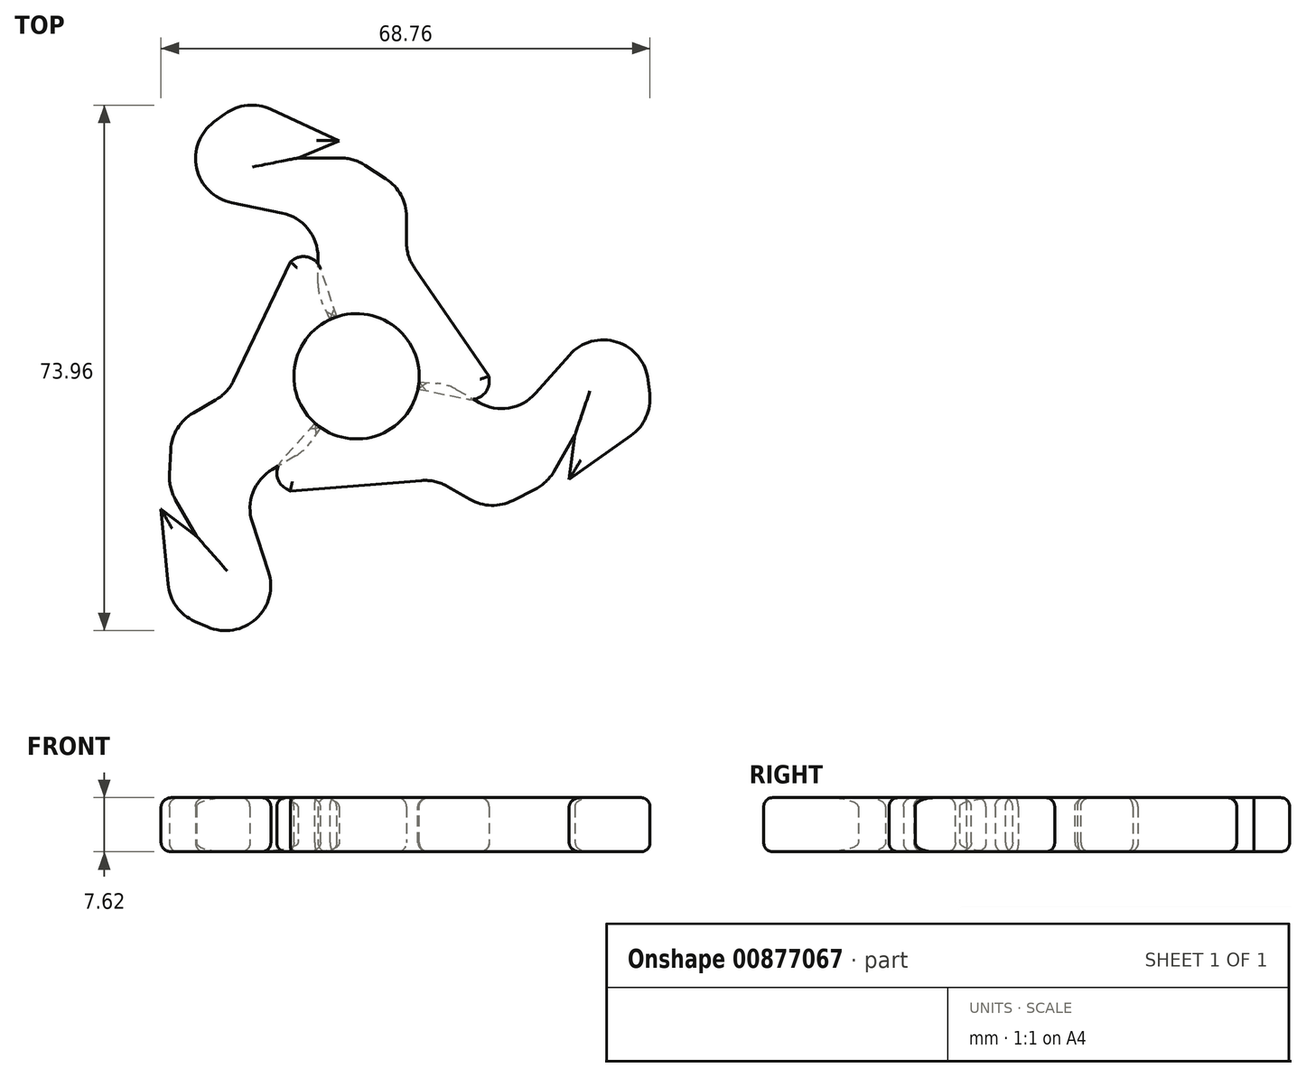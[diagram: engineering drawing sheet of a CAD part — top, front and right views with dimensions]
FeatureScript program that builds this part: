
annotation { "Feature Type Name" : "Feature", "Feature Type Description" : "" }
export const myFeature = defineFeature(function(context is Context, id is Id, definition is map)
    precondition{}
    {
        {
            var Q0;
            Q0=qCreatedBy(makeId("Top.planeOp"),FACE);
            var sketch = newSketch(context, id + "F0", { "sketchPlane" : qUnion([Q0])});
            skLineSegment(sketch, "E0", {"start": v(-31.2, 32.55) * mm, "end": v(-29.62, 33.7) * mm});
            skLineSegment(sketch, "E1", {"start": v(-23.2, 34.37) * mm, "end": v(-13.55, 29.92) * mm});
            skLineSegment(sketch, "E2", {"start": v(-13.55, 29.92) * mm, "end": v(-19.38, 27.5) * mm});
            skLineSegment(sketch, "E3", {"start": v(-19.38, 27.5) * mm, "end": v(-13.42, 27.5) * mm});
            skLineSegment(sketch, "E4", {"start": v(-9.97, 26.48) * mm, "end": v(-7.01, 24.57) * mm});
            skLineSegment(sketch, "E5", {"start": v(-4.12, 19.24) * mm, "end": v(-4.12, 15.63) * mm});
            skLineSegment(sketch, "E6", {"start": v(-3, 12.03) * mm, "end": v(7.5, -3.22) * mm});
            skLineSegment(sketch, "E7", {"start": v(7.5, -3.22) * mm, "end": v(-11.14, -3.22) * mm});
            skLineSegment(sketch, "E8", {"start": v(-11.14, -3.22) * mm, "end": v(-15.97, 7.16) * mm});
            skLineSegment(sketch, "E9", {"start": v(-16.56, 9.84) * mm, "end": v(-16.56, 13.55) * mm});
            skLineSegment(sketch, "E10", {"start": v(-21.64, 19.77) * mm, "end": v(-28.7, 21.22) * mm});
            skLineSegment(sketch, "E11", {"start": v(-11.14, -3.22) * mm, "end": v(4.46, -6.42) * mm});
            skLineSegment(sketch, "E12", {"start": v(7.51, -3.86) * mm, "end": v(7.5, -3.22) * mm});
            skPoint(sketch, "E13.visualSharp", {"position": v(-16.56, 18.73) * mm});
            skArc(sketch, "E13.filletArc", {"start": v(-16.56, 13.55) * mm, "mid": v(-18, 17.56) * mm, "end": v(-21.64, 19.77) * mm});
            skPoint(sketch, "E14.visualSharp", {"position": v(-16.56, 8.43) * mm});
            skArc(sketch, "E14.filletArc", {"start": v(-16.56, 9.84) * mm, "mid": v(-16.41, 8.47) * mm, "end": v(-15.97, 7.16) * mm});
            skPoint(sketch, "E15.visualSharp", {"position": v(-4.12, 13.65) * mm});
            skArc(sketch, "E15.filletArc", {"start": v(-4.12, 15.63) * mm, "mid": v(-3.83, 13.74) * mm, "end": v(-3, 12.03) * mm});
            skPoint(sketch, "E16.visualSharp", {"position": v(-4.12, 22.69) * mm});
            skArc(sketch, "E16.filletArc", {"start": v(-4.12, 19.24) * mm, "mid": v(-4.89, 22.27) * mm, "end": v(-7.01, 24.57) * mm});
            skPoint(sketch, "E17.visualSharp", {"position": v(-11.54, 27.5) * mm});
            skArc(sketch, "E17.filletArc", {"start": v(-9.97, 26.48) * mm, "mid": v(-11.62, 27.25) * mm, "end": v(-13.42, 27.5) * mm});
            skPoint(sketch, "E18.visualSharp", {"position": v(-26.6, 35.94) * mm});
            skArc(sketch, "E18.filletArc", {"start": v(-23.2, 34.37) * mm, "mid": v(-26.5, 34.92) * mm, "end": v(-29.62, 33.7) * mm});
            skPoint(sketch, "E19.visualSharp", {"position": v(7.6, -7.07) * mm});
            skArc(sketch, "E19.filletArc", {"start": v(4.46, -6.42) * mm, "mid": v(6.6, -5.88) * mm, "end": v(7.51, -3.86) * mm});
            skPoint(sketch, "E20.visualSharp", {"position": v(-42.67, 24.08) * mm});
            skArc(sketch, "E20.filletArc", {"start": v(-31.2, 32.55) * mm, "mid": v(-33.63, 26.07) * mm, "end": v(-28.7, 21.22) * mm});
            skSolve(sketch);
        }
        {
            var Q0;
            Q0=makeQuery(id+"F0.imprint","IMPRINT",FACE,{"disambiguationData":[TD([[makeQuery(id+"F0.imprint","IMPRINT",EDGE,{"derivedFrom":sQuery(id+"F0.wireOp",EDGE,"E0")}),-1.0]])]});
            var Q1;
            Q1=makeQuery(id+"F0.imprint","IMPRINT",FACE,{"disambiguationData":[TD([[makeQuery(id+"F0.imprint","IMPRINT",EDGE,{"derivedFrom":sQuery(id+"F0.wireOp",EDGE,"E7")}),1.0]])]});
            extrude(context, id + "F1", {"entities" : qUnion([Q0, Q1]), "depth" : 7.62 * mm, "offsetDistance" : 25.4 * mm});
        }
        {
            var Q0;
            Q0=makeQuery(id+"F1.opExtrude","SWEPT_BODY",BODY,{"disambiguationData":[OSD([sQuery(id+"F0.wireOp",EDGE,"E0"),sQuery(id+"F0.wireOp",EDGE,"E1"),sQuery(id+"F0.wireOp",EDGE,"E2"),sQuery(id+"F0.wireOp",EDGE,"E3"),sQuery(id+"F0.wireOp",EDGE,"E4"),sQuery(id+"F0.wireOp",EDGE,"E5"),sQuery(id+"F0.wireOp",EDGE,"E6"),sQuery(id+"F0.wireOp",EDGE,"E7"),sQuery(id+"F0.wireOp",EDGE,"E8"),sQuery(id+"F0.wireOp",EDGE,"E9"),sQuery(id+"F0.wireOp",EDGE,"E10")])]});
            var Q1;
            Q1=makeQuery(id+"F1.opExtrude","SWEPT_EDGE",EDGE,{"disambiguationData":[OSD([sQuery(id+"F0.wireOp",EDGE,"E7"),sQuery(id+"F0.wireOp",EDGE,"E8")])]});
            circularPattern(context, id + "F2", {"entities" : qUnion([Q0]), "axis" : qUnion([Q1]), "angle" : 360 * degree, "instanceCount" : 3, "equalSpace" : true});
        }
        {
            var Q0;
            Q0=makeQuery(id+"F1.opExtrude","CAP_FACE",FACE,{"disambiguationData":[OSD([sQuery(id+"F0.wireOp",EDGE,"E0"),sQuery(id+"F0.wireOp",EDGE,"E1"),sQuery(id+"F0.wireOp",EDGE,"E2"),sQuery(id+"F0.wireOp",EDGE,"E3"),sQuery(id+"F0.wireOp",EDGE,"E4"),sQuery(id+"F0.wireOp",EDGE,"E5"),sQuery(id+"F0.wireOp",EDGE,"E6"),sQuery(id+"F0.wireOp",EDGE,"E8"),sQuery(id+"F0.wireOp",EDGE,"E9"),sQuery(id+"F0.wireOp",EDGE,"E10"),sQuery(id+"F0.wireOp",EDGE,"E11"),sQuery(id+"F0.wireOp",EDGE,"E12")])],"isStart":false});
            var sketch = newSketch(context, id + "F3", { "sketchPlane" : qUnion([Q0])});
            skCircle(sketch, "E21", {"center": v(-11.14, -3.22) * mm, "radius": 8.82 * mm});
            skSolve(sketch);
        }
        {
            var Q0;
            Q0 = qSketchRegion(id + "F3", true);
            extrude(context, id + "F4", {"entities" : qUnion([Q0]), "operationType" : NewBodyOperationType.REMOVE, "oppositeDirection" : true, "depth" : 25.4 * mm, "offsetDistance" : 25.4 * mm});
        }
        {
            var Q0;
            Q0=makeQuery(id+"F2.opPattern","COPY",EDGE,{"derivedFrom":makeQuery(id+"F1.opExtrude","CAP_EDGE",EDGE,{"disambiguationData":[OSD([sQuery(id+"F0.wireOp",EDGE,"E15.filletArc")])],"isStart":false}),"instanceName":"2"});
            var Q1;
            Q1=makeQuery(id+"F2.opPattern","COPY",EDGE,{"derivedFrom":makeQuery(id+"F1.opExtrude","CAP_EDGE",EDGE,{"disambiguationData":[OSD([sQuery(id+"F0.wireOp",EDGE,"E1")])],"isStart":false}),"instanceName":"2"});
            var Q2;
            Q2=makeQuery(id+"F2.opPattern","COPY",EDGE,{"derivedFrom":makeQuery(id+"F1.opExtrude","CAP_EDGE",EDGE,{"disambiguationData":[OSD([sQuery(id+"F0.wireOp",EDGE,"E20.filletArc")])],"isStart":false}),"instanceName":"2"});
            var Q3;
            Q3=makeQuery(id+"F2.opPattern","COPY",EDGE,{"derivedFrom":makeQuery(id+"F1.opExtrude","CAP_EDGE",EDGE,{"disambiguationData":[OSD([sQuery(id+"F0.wireOp",EDGE,"E6")])],"isStart":false}),"instanceName":"1"});
            var Q4;
            Q4=makeQuery(id+"F1.opExtrude","CAP_EDGE",EDGE,{"disambiguationData":[OSD([sQuery(id+"F0.wireOp",EDGE,"E20.filletArc")])],"isStart":false});
            var Q5;
            Q5=makeQuery(id+"F2.opPattern","COPY",FACE,{"derivedFrom":makeQuery(id+"F1.opExtrude","CAP_FACE",FACE,{"disambiguationData":[OSD([sQuery(id+"F0.wireOp",EDGE,"E0"),sQuery(id+"F0.wireOp",EDGE,"E1"),sQuery(id+"F0.wireOp",EDGE,"E2"),sQuery(id+"F0.wireOp",EDGE,"E3"),sQuery(id+"F0.wireOp",EDGE,"E4"),sQuery(id+"F0.wireOp",EDGE,"E5"),sQuery(id+"F0.wireOp",EDGE,"E6"),sQuery(id+"F0.wireOp",EDGE,"E8"),sQuery(id+"F0.wireOp",EDGE,"E9"),sQuery(id+"F0.wireOp",EDGE,"E10"),sQuery(id+"F0.wireOp",EDGE,"E11"),sQuery(id+"F0.wireOp",EDGE,"E12"),sQuery(id+"F0.wireOp",EDGE,"E13.filletArc"),sQuery(id+"F0.wireOp",EDGE,"E14.filletArc"),sQuery(id+"F0.wireOp",EDGE,"E15.filletArc"),sQuery(id+"F0.wireOp",EDGE,"E16.filletArc"),sQuery(id+"F0.wireOp",EDGE,"E17.filletArc"),sQuery(id+"F0.wireOp",EDGE,"E18.filletArc"),sQuery(id+"F0.wireOp",EDGE,"E19.filletArc"),sQuery(id+"F0.wireOp",EDGE,"E20.filletArc")])],"isStart":false}),"instanceName":"2"});
            var Q6;
            Q6=makeQuery(id+"F2.opPattern","COPY",FACE,{"derivedFrom":makeQuery(id+"F1.opExtrude","CAP_FACE",FACE,{"disambiguationData":[OSD([sQuery(id+"F0.wireOp",EDGE,"E0"),sQuery(id+"F0.wireOp",EDGE,"E1"),sQuery(id+"F0.wireOp",EDGE,"E2"),sQuery(id+"F0.wireOp",EDGE,"E3"),sQuery(id+"F0.wireOp",EDGE,"E4"),sQuery(id+"F0.wireOp",EDGE,"E5"),sQuery(id+"F0.wireOp",EDGE,"E6"),sQuery(id+"F0.wireOp",EDGE,"E8"),sQuery(id+"F0.wireOp",EDGE,"E9"),sQuery(id+"F0.wireOp",EDGE,"E10"),sQuery(id+"F0.wireOp",EDGE,"E11"),sQuery(id+"F0.wireOp",EDGE,"E12"),sQuery(id+"F0.wireOp",EDGE,"E13.filletArc"),sQuery(id+"F0.wireOp",EDGE,"E14.filletArc"),sQuery(id+"F0.wireOp",EDGE,"E15.filletArc"),sQuery(id+"F0.wireOp",EDGE,"E16.filletArc"),sQuery(id+"F0.wireOp",EDGE,"E17.filletArc"),sQuery(id+"F0.wireOp",EDGE,"E18.filletArc"),sQuery(id+"F0.wireOp",EDGE,"E19.filletArc"),sQuery(id+"F0.wireOp",EDGE,"E20.filletArc")])],"isStart":false}),"instanceName":"1"});
            var Q7;
            Q7=makeQuery(id+"F1.opExtrude","CAP_FACE",FACE,{"disambiguationData":[OSD([sQuery(id+"F0.wireOp",EDGE,"E0"),sQuery(id+"F0.wireOp",EDGE,"E1"),sQuery(id+"F0.wireOp",EDGE,"E2"),sQuery(id+"F0.wireOp",EDGE,"E3"),sQuery(id+"F0.wireOp",EDGE,"E4"),sQuery(id+"F0.wireOp",EDGE,"E5"),sQuery(id+"F0.wireOp",EDGE,"E6"),sQuery(id+"F0.wireOp",EDGE,"E8"),sQuery(id+"F0.wireOp",EDGE,"E9"),sQuery(id+"F0.wireOp",EDGE,"E10"),sQuery(id+"F0.wireOp",EDGE,"E11"),sQuery(id+"F0.wireOp",EDGE,"E12"),sQuery(id+"F0.wireOp",EDGE,"E13.filletArc"),sQuery(id+"F0.wireOp",EDGE,"E14.filletArc"),sQuery(id+"F0.wireOp",EDGE,"E15.filletArc"),sQuery(id+"F0.wireOp",EDGE,"E16.filletArc"),sQuery(id+"F0.wireOp",EDGE,"E17.filletArc"),sQuery(id+"F0.wireOp",EDGE,"E18.filletArc"),sQuery(id+"F0.wireOp",EDGE,"E19.filletArc"),sQuery(id+"F0.wireOp",EDGE,"E20.filletArc")])],"isStart":false});
            var Q8;
            Q8=makeQuery(id+"F2.opPattern","COPY",FACE,{"derivedFrom":makeQuery(id+"F1.opExtrude","CAP_FACE",FACE,{"disambiguationData":[OSD([sQuery(id+"F0.wireOp",EDGE,"E0"),sQuery(id+"F0.wireOp",EDGE,"E1"),sQuery(id+"F0.wireOp",EDGE,"E2"),sQuery(id+"F0.wireOp",EDGE,"E3"),sQuery(id+"F0.wireOp",EDGE,"E4"),sQuery(id+"F0.wireOp",EDGE,"E5"),sQuery(id+"F0.wireOp",EDGE,"E6"),sQuery(id+"F0.wireOp",EDGE,"E8"),sQuery(id+"F0.wireOp",EDGE,"E9"),sQuery(id+"F0.wireOp",EDGE,"E10"),sQuery(id+"F0.wireOp",EDGE,"E11"),sQuery(id+"F0.wireOp",EDGE,"E12"),sQuery(id+"F0.wireOp",EDGE,"E13.filletArc"),sQuery(id+"F0.wireOp",EDGE,"E14.filletArc"),sQuery(id+"F0.wireOp",EDGE,"E15.filletArc"),sQuery(id+"F0.wireOp",EDGE,"E16.filletArc"),sQuery(id+"F0.wireOp",EDGE,"E17.filletArc"),sQuery(id+"F0.wireOp",EDGE,"E18.filletArc"),sQuery(id+"F0.wireOp",EDGE,"E19.filletArc"),sQuery(id+"F0.wireOp",EDGE,"E20.filletArc")])],"isStart":true}),"instanceName":"2"});
            var Q9;
            Q9=makeQuery(id+"F1.opExtrude","CAP_FACE",FACE,{"disambiguationData":[OSD([sQuery(id+"F0.wireOp",EDGE,"E0"),sQuery(id+"F0.wireOp",EDGE,"E1"),sQuery(id+"F0.wireOp",EDGE,"E2"),sQuery(id+"F0.wireOp",EDGE,"E3"),sQuery(id+"F0.wireOp",EDGE,"E4"),sQuery(id+"F0.wireOp",EDGE,"E5"),sQuery(id+"F0.wireOp",EDGE,"E6"),sQuery(id+"F0.wireOp",EDGE,"E8"),sQuery(id+"F0.wireOp",EDGE,"E9"),sQuery(id+"F0.wireOp",EDGE,"E10"),sQuery(id+"F0.wireOp",EDGE,"E11"),sQuery(id+"F0.wireOp",EDGE,"E12"),sQuery(id+"F0.wireOp",EDGE,"E13.filletArc"),sQuery(id+"F0.wireOp",EDGE,"E14.filletArc"),sQuery(id+"F0.wireOp",EDGE,"E15.filletArc"),sQuery(id+"F0.wireOp",EDGE,"E16.filletArc"),sQuery(id+"F0.wireOp",EDGE,"E17.filletArc"),sQuery(id+"F0.wireOp",EDGE,"E18.filletArc"),sQuery(id+"F0.wireOp",EDGE,"E19.filletArc"),sQuery(id+"F0.wireOp",EDGE,"E20.filletArc")])],"isStart":true});
            var Q10;
            Q10=makeQuery(id+"F2.opPattern","COPY",FACE,{"derivedFrom":makeQuery(id+"F1.opExtrude","CAP_FACE",FACE,{"disambiguationData":[OSD([sQuery(id+"F0.wireOp",EDGE,"E0"),sQuery(id+"F0.wireOp",EDGE,"E1"),sQuery(id+"F0.wireOp",EDGE,"E2"),sQuery(id+"F0.wireOp",EDGE,"E3"),sQuery(id+"F0.wireOp",EDGE,"E4"),sQuery(id+"F0.wireOp",EDGE,"E5"),sQuery(id+"F0.wireOp",EDGE,"E6"),sQuery(id+"F0.wireOp",EDGE,"E8"),sQuery(id+"F0.wireOp",EDGE,"E9"),sQuery(id+"F0.wireOp",EDGE,"E10"),sQuery(id+"F0.wireOp",EDGE,"E11"),sQuery(id+"F0.wireOp",EDGE,"E12"),sQuery(id+"F0.wireOp",EDGE,"E13.filletArc"),sQuery(id+"F0.wireOp",EDGE,"E14.filletArc"),sQuery(id+"F0.wireOp",EDGE,"E15.filletArc"),sQuery(id+"F0.wireOp",EDGE,"E16.filletArc"),sQuery(id+"F0.wireOp",EDGE,"E17.filletArc"),sQuery(id+"F0.wireOp",EDGE,"E18.filletArc"),sQuery(id+"F0.wireOp",EDGE,"E19.filletArc"),sQuery(id+"F0.wireOp",EDGE,"E20.filletArc")])],"isStart":true}),"instanceName":"1"});
            fillet(context, id + "F5", {"entities" : qUnion([Q0, Q1, Q2, Q3, Q4, Q5, Q6, Q7, Q8, Q9, Q10]), "radius" : 1.27 * mm, "tangentPropagation" : true, "allowEdgeOverflow" : false});
        }
    });
